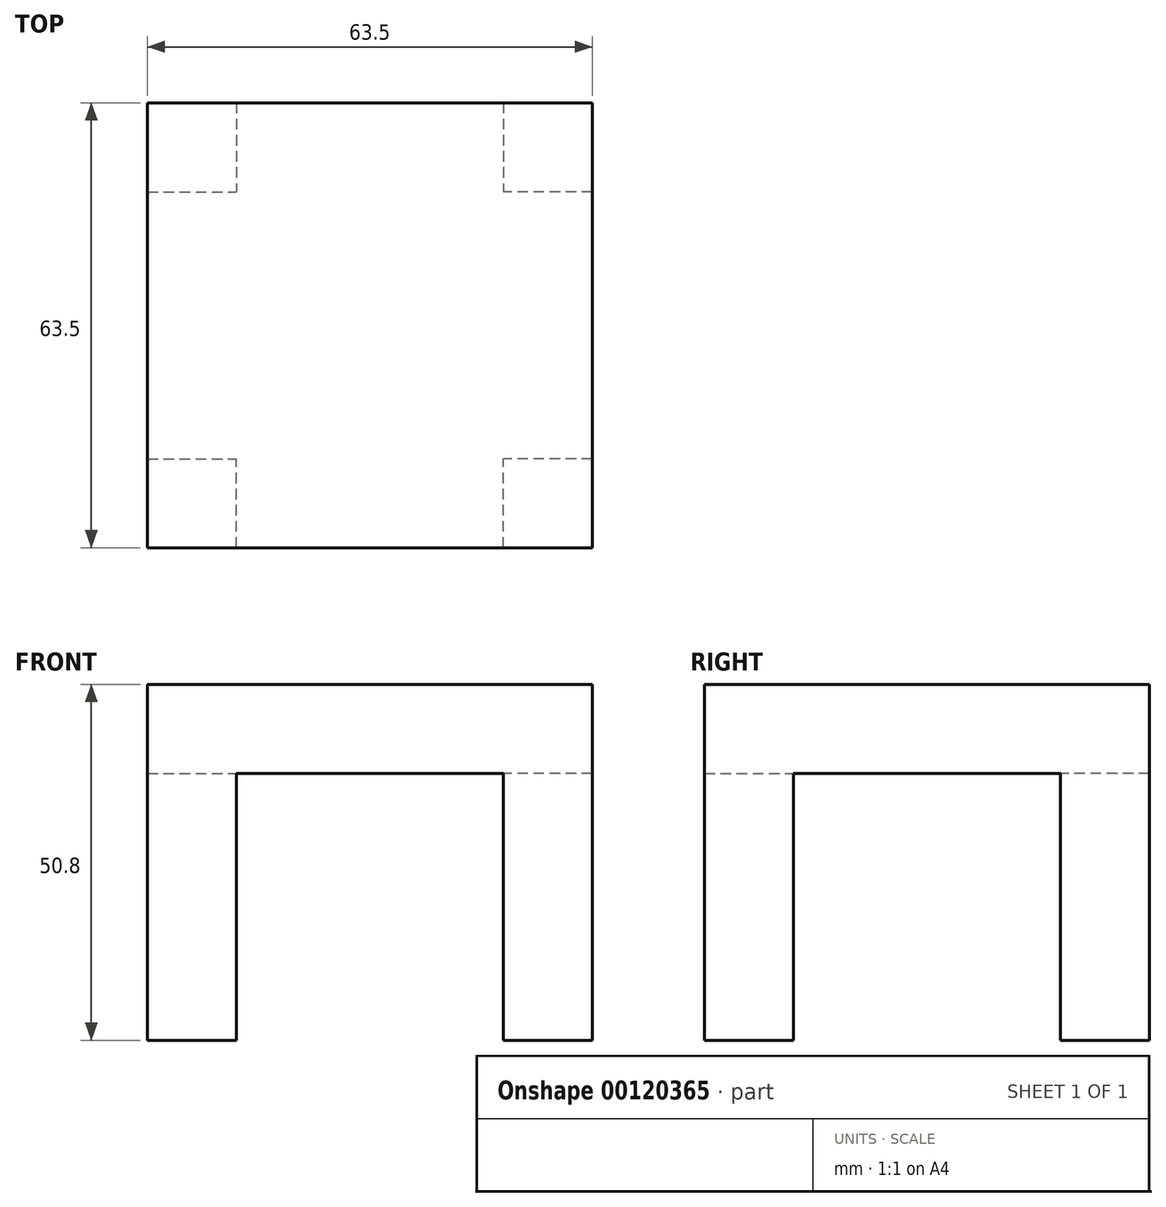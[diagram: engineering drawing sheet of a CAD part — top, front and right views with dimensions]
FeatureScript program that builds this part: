
annotation { "Feature Type Name" : "Feature", "Feature Type Description" : "" }
export const myFeature = defineFeature(function(context is Context, id is Id, definition is map)
    precondition{}
    {
        {
            var Q0;
            Q0=qCreatedBy(makeId("Top.planeOp"),FACE);
            var sketch = newSketch(context, id + "F0", { "sketchPlane" : qUnion([Q0])});
            skLineSegment(sketch, "E0.bottom", {"start": v(31.75, 31.75) * mm, "end": v(-31.75, 31.75) * mm});
            skLineSegment(sketch, "E0.top", {"start": v(31.75, -31.75) * mm, "end": v(-31.75, -31.75) * mm});
            skLineSegment(sketch, "E0.left", {"start": v(31.75, 31.75) * mm, "end": v(31.75, -31.75) * mm});
            skLineSegment(sketch, "E0.right", {"start": v(-31.75, 31.75) * mm, "end": v(-31.75, -31.75) * mm});
            skPoint(sketch, "E0.middle", {"position": v(0, 0) * mm});
            skSolve(sketch);
        }
        {
            var Q0;
            Q0 = qSketchRegion(id + "F0", true);
            extrude(context, id + "F1", {"entities" : qUnion([Q0]), "depth" : 12.7 * mm});
        }
        {
            var Q0;
            Q0=makeQuery(id+"F1.opExtrude","CAP_FACE",FACE,{"disambiguationData":[OSD([sQuery(id+"F0.wireOp",EDGE,"E0.bottom"),sQuery(id+"F0.wireOp",EDGE,"E0.top"),sQuery(id+"F0.wireOp",EDGE,"E0.left"),sQuery(id+"F0.wireOp",EDGE,"E0.right")])],"isStart":true});
            var sketch = newSketch(context, id + "F2", { "sketchPlane" : qUnion([Q0])});
            skLineSegment(sketch, "E1.bottom", {"start": v(-31.75, 31.75) * mm, "end": v(-19.05, 31.75) * mm});
            skLineSegment(sketch, "E1.top", {"start": v(-31.75, 19.05) * mm, "end": v(-19.05, 19.05) * mm});
            skLineSegment(sketch, "E1.left", {"start": v(-31.75, 31.75) * mm, "end": v(-31.75, 19.05) * mm});
            skLineSegment(sketch, "E1.right", {"start": v(-19.05, 31.75) * mm, "end": v(-19.05, 19.05) * mm});
            skLineSegment(sketch, "E2.bottom", {"start": v(31.75, 31.75) * mm, "end": v(19.05, 31.75) * mm});
            skLineSegment(sketch, "E2.top", {"start": v(31.75, 19.05) * mm, "end": v(19.05, 19.05) * mm});
            skLineSegment(sketch, "E2.left", {"start": v(31.75, 31.75) * mm, "end": v(31.75, 19.05) * mm});
            skLineSegment(sketch, "E2.right", {"start": v(19.05, 31.75) * mm, "end": v(19.05, 19.05) * mm});
            skLineSegment(sketch, "E3.bottom", {"start": v(31.75, -31.75) * mm, "end": v(19.05, -31.75) * mm});
            skLineSegment(sketch, "E3.top", {"start": v(31.75, -19.05) * mm, "end": v(19.05, -19.05) * mm});
            skLineSegment(sketch, "E3.left", {"start": v(31.75, -31.75) * mm, "end": v(31.75, -19.05) * mm});
            skLineSegment(sketch, "E3.right", {"start": v(19.05, -31.75) * mm, "end": v(19.05, -19.05) * mm});
            skLineSegment(sketch, "E4.bottom", {"start": v(-31.75, -31.75) * mm, "end": v(-19.05, -31.75) * mm});
            skLineSegment(sketch, "E4.top", {"start": v(-31.75, -19.05) * mm, "end": v(-19.05, -19.05) * mm});
            skLineSegment(sketch, "E4.left", {"start": v(-31.75, -31.75) * mm, "end": v(-31.75, -19.05) * mm});
            skLineSegment(sketch, "E4.right", {"start": v(-19.05, -31.75) * mm, "end": v(-19.05, -19.05) * mm});
            skSolve(sketch);
        }
        {
            var Q0;
            Q0 = qSketchRegion(id + "F2", true);
            extrude(context, id + "F3", {"entities" : qUnion([Q0]), "operationType" : NewBodyOperationType.ADD, "depth" : 38.1 * mm});
        }
    });
